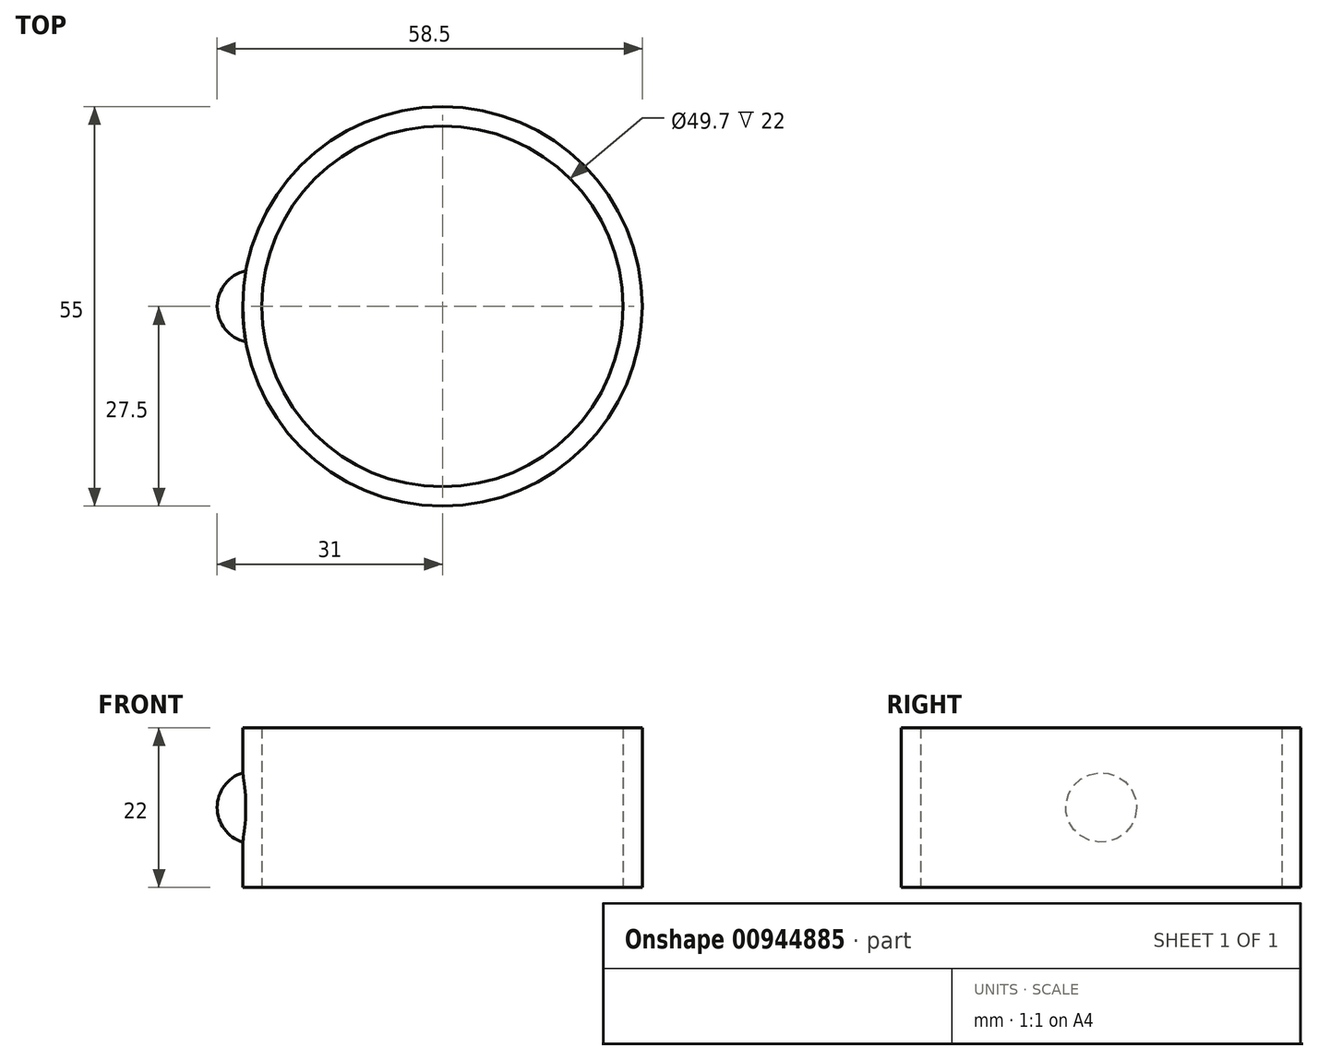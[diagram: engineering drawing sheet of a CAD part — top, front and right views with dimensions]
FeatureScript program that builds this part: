
annotation { "Feature Type Name" : "Feature", "Feature Type Description" : "" }
export const myFeature = defineFeature(function(context is Context, id is Id, definition is map)
    precondition{}
    {
        {
            var Q0;
            Q0=qCreatedBy(makeId("Top.planeOp"),FACE);
            var sketch = newSketch(context, id + "F0", { "sketchPlane" : qUnion([Q0])});
            skCircle(sketch, "E0", {"center": v(0, 0) * mm, "radius": 27.5 * mm});
            skCircle(sketch, "E1.0", {"center": v(0, 0) * mm, "radius": 24.85 * mm});
            skSolve(sketch);
        }
        {
            var Q0;
            Q0 = qSketchRegion(id + "F0", true);
            extrude(context, id + "F1", {"entities" : qUnion([Q0]), "depth" : 22 * mm, "offsetDistance" : 25 * mm});
        }
        {
            var Q0;
            Q0=qCreatedBy(makeId("Front.planeOp"),FACE);
            var sketch = newSketch(context, id + "F2", { "sketchPlane" : qUnion([Q0])});
            skArc(sketch, "E2", {"start": v(-26, 16) * mm, "mid": v(-31, 11) * mm, "end": v(-26, 6) * mm});
            skLineSegment(sketch, "E3", {"start": v(-26, 6) * mm, "end": v(-26, 16) * mm});
            skSolve(sketch);
        }
        {
            var Q0;
            Q0=makeQuery(id+"F2.imprint","IMPRINT",FACE,{"disambiguationData":[TD([[makeQuery(id+"F2.imprint","IMPRINT",EDGE,{"derivedFrom":sQuery(id+"F2.wireOp",EDGE,"E2")}),1.0]])]});
            var Q1;
            Q1=sQuery(id+"F2.wireOp",EDGE,"E2");
            var Q2;
            Q2=sQuery(id+"F2.wireOp",EDGE,"E3");
            revolve(context, id + "F3", {"operationType" : NewBodyOperationType.ADD, "surfaceOperationType" : NewSurfaceOperationType.NEW, "entities" : qUnion([Q0]), "surfaceEntities" : qUnion([Q1]), "axis" : qUnion([Q2]), "revolveType" : RevolveType.FULL});
        }
        {
            var Q0;
            Q0=qCreatedBy(makeId("Top.planeOp"),FACE);
            var sketch = newSketch(context, id + "F4", { "sketchPlane" : qUnion([Q0])});
            skCircle(sketch, "E4", {"center": v(0, 0) * mm, "radius": 24.85 * mm});
            skSolve(sketch);
        }
        {
            var Q0;
            Q0 = qSketchRegion(id + "F4", true);
            extrude(context, id + "F5", {"entities" : qUnion([Q0]), "operationType" : NewBodyOperationType.REMOVE, "depth" : 25 * mm, "offsetDistance" : 25 * mm});
        }
    });
